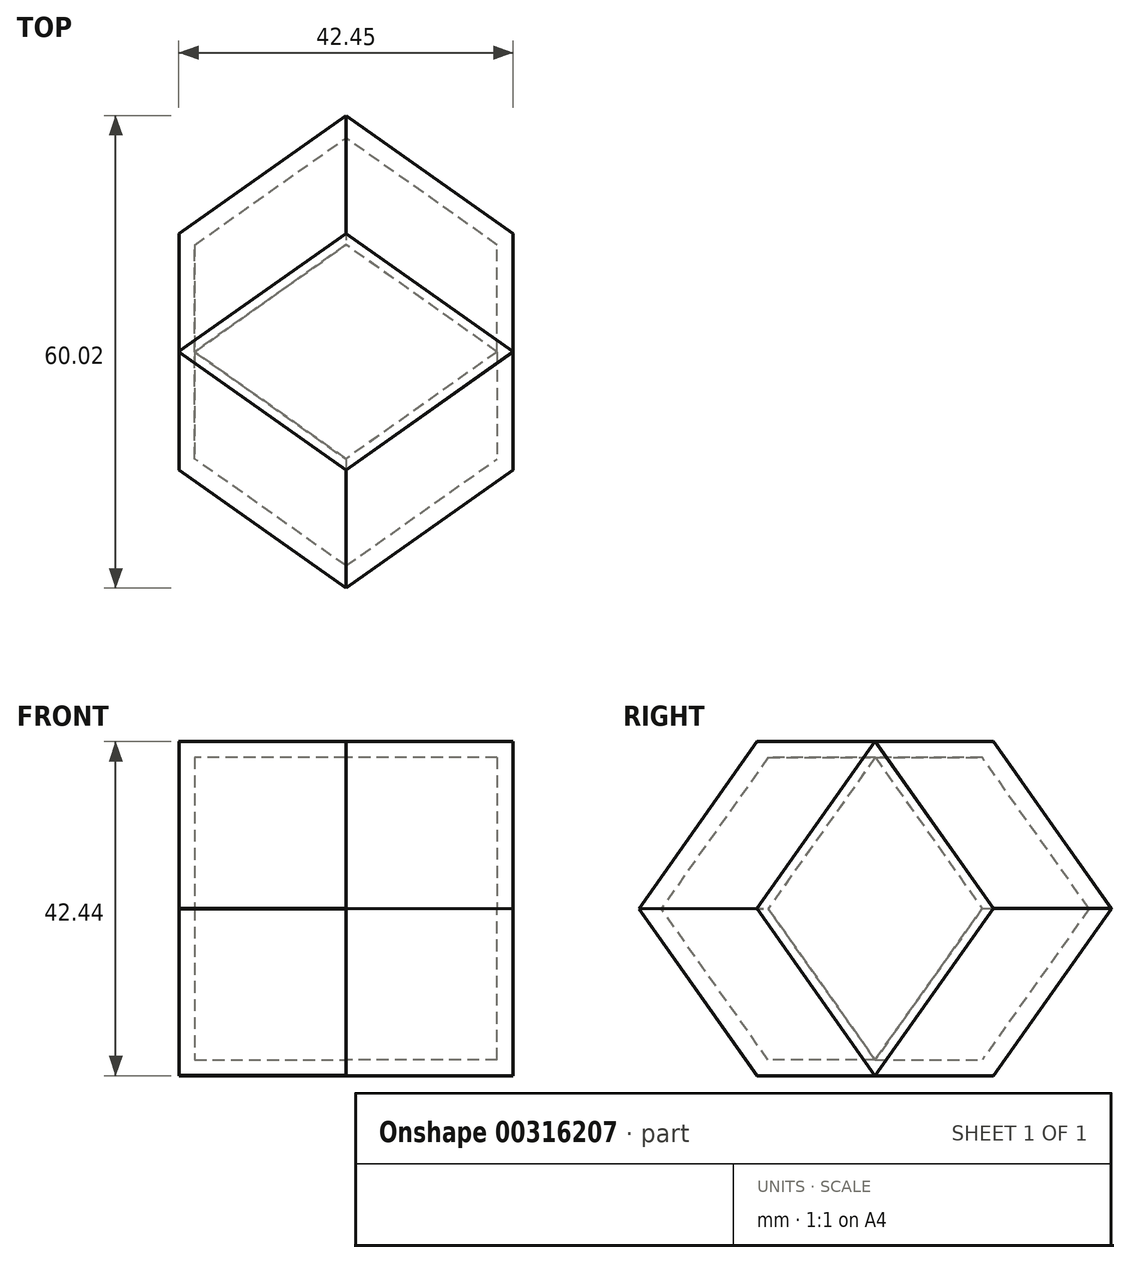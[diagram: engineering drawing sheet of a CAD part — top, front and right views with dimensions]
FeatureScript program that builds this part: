
annotation { "Feature Type Name" : "Feature", "Feature Type Description" : "" }
export const myFeature = defineFeature(function(context is Context, id is Id, definition is map)
    precondition{}
    {
        {
            var Q0;
            Q0=qCreatedBy(makeId("Top.planeOp"),FACE);
            var sketch = newSketch(context, id + "F0", { "sketchPlane" : qUnion([Q0])});
            skLineSegment(sketch, "E0", {"start": v(0, 15) * mm, "end": v(-21.22, 0) * mm});
            skLineSegment(sketch, "E1", {"start": v(-21.22, 0) * mm, "end": v(0, -15) * mm});
            skLineSegment(sketch, "E2", {"start": v(0, -15) * mm, "end": v(21.22, 0) * mm});
            skLineSegment(sketch, "E3", {"start": v(21.22, 0) * mm, "end": v(0, 15) * mm});
            skSolve(sketch);
        }
        {
            var Q0;
            Q0 = qSketchRegion(id + "F0", true);
            extrude(context, id + "F1", {"entities" : qUnion([Q0]), "depth" : 2 * mm, "hasDraft" : true, "draftAngle" : 15 * degree, "draftPullDirection" : true});
        }
        {
            var Q0;
            Q0=qCreatedBy(makeId("Right.planeOp"),FACE);
            var Q1;
            Q1=makeQuery(id+"F1.opExtrude","CAP_VERTEX",VERTEX,{"disambiguationData":[OSD([sQuery(id+"F0.wireOp",EDGE,"E2"),sQuery(id+"F0.wireOp",EDGE,"E3")])],"isStart":true});
            cPlane(context, id + "F2", {"entities" : qUnion([Q0, Q1]), "cplaneType" : CPlaneType.PLANE_POINT, "offset" : 25 * mm, "width" : 150 * mm, "height" : 150 * mm});
        }
        {
            var Q0;
            Q0=qCreatedBy(id+"F2.planeOp",FACE);
            var sketch = newSketch(context, id + "F3", { "sketchPlane" : qUnion([Q0])});
            skLineSegment(sketch, "E4.0", {"start": v(0, 0) * mm, "end": v(15, 0) * mm, "construction": true});
            skLineSegment(sketch, "E5", {"start": v(0, 0) * mm, "end": v(0, 42.44) * mm, "construction": true});
            skLineSegment(sketch, "E6", {"start": v(0, 0) * mm, "end": v(15, 21.22) * mm});
            skLineSegment(sketch, "E7", {"start": v(15, 21.22) * mm, "end": v(0, 42.44) * mm});
            skLineSegment(sketch, "E8", {"start": v(15, 21.22) * mm, "end": v(-15, 21.22) * mm, "construction": true});
            skLineSegment(sketch, "E9", {"start": v(0, 0) * mm, "end": v(-15, 21.22) * mm});
            skLineSegment(sketch, "E10", {"start": v(-15, 21.22) * mm, "end": v(0, 42.44) * mm});
            skSolve(sketch);
        }
        {
            var Q0;
            Q0 = qSketchRegion(id + "F3", true);
            extrude(context, id + "F4", {"entities" : qUnion([Q0]), "operationType" : NewBodyOperationType.ADD, "oppositeDirection" : true, "depth" : 2 * mm, "hasDraft" : true, "draftAngle" : 15 * degree, "draftPullDirection" : true});
        }
        {
            var Q0;
            Q0=makeQuery(id+"F1.opExtrude","CAP_VERTEX",VERTEX,{"disambiguationData":[OSD([sQuery(id+"F0.wireOp",EDGE,"E2"),sQuery(id+"F0.wireOp",EDGE,"E3")])],"isStart":true});
            var Q1;
            Q1=makeQuery(id+"F4.opExtrude","CAP_VERTEX",VERTEX,{"disambiguationData":[OSD([sQuery(id+"F3.wireOp",EDGE,"E9"),sQuery(id+"F3.wireOp",EDGE,"E10")])],"isStart":true});
            var Q2;
            Q2=makeQuery(id+"F1.opExtrude","CAP_VERTEX",VERTEX,{"disambiguationData":[OSD([sQuery(id+"F0.wireOp",EDGE,"E1"),sQuery(id+"F0.wireOp",EDGE,"E2")])],"isStart":true});
            cPlane(context, id + "F5", {"entities" : qUnion([Q0, Q1, Q2]), "cplaneType" : CPlaneType.THREE_POINT, "offset" : 25 * mm, "width" : 150 * mm, "height" : 150 * mm});
        }
        {
            var Q0;
            Q0=qCreatedBy(id+"F5.planeOp",FACE);
            var sketch = newSketch(context, id + "F6", { "sketchPlane" : qUnion([Q0])});
            skLineSegment(sketch, "E11.0", {"start": v(-18.38, 0) * mm, "end": v(-18.38, 25.99) * mm});
            skLineSegment(sketch, "E12.0", {"start": v(6.12, 8.66) * mm, "end": v(-18.38, 0) * mm});
            skLineSegment(sketch, "E13", {"start": v(-18.38, 25.99) * mm, "end": v(6.12, 8.66) * mm, "construction": true});
            skLineSegment(sketch, "E14", {"start": v(-18.38, 25.99) * mm, "end": v(6.12, 34.64) * mm});
            skLineSegment(sketch, "E15", {"start": v(6.12, 34.64) * mm, "end": v(6.12, 8.66) * mm});
            skSolve(sketch);
        }
        {
            var Q0;
            Q0 = qSketchRegion(id + "F6", true);
            extrude(context, id + "F7", {"entities" : qUnion([Q0]), "operationType" : NewBodyOperationType.ADD, "depth" : 2 * mm, "hasDraft" : true, "draftAngle" : 15 * degree, "draftPullDirection" : true});
        }
        {
            var Q0;
            Q0=makeQuery(id+"F7.boolean.opBoolean","MERGE",VERTEX,{"derivedFrom":[makeQuery(id+"F4.boolean.opBoolean","MERGE",VERTEX,{"derivedFrom":[makeQuery(id+"F1.opExtrude","CAP_VERTEX",VERTEX,{"disambiguationData":[OSD([sQuery(id+"F0.wireOp",EDGE,"E2"),sQuery(id+"F0.wireOp",EDGE,"E3")])],"isStart":true}),makeQuery(id+"F4.opExtrude","CAP_VERTEX",VERTEX,{"disambiguationData":[OSD([sQuery(id+"F3.wireOp",EDGE,"E6"),sQuery(id+"F3.wireOp",EDGE,"E9")])],"isStart":true})]}),makeQuery(id+"F7.opExtrude","CAP_VERTEX",VERTEX,{"disambiguationData":[OSD([sQuery(id+"F6.wireOp",EDGE,"E11.0"),sQuery(id+"F6.wireOp",EDGE,"E12.0")])],"isStart":true})]});
            var Q1;
            Q1=makeQuery(id+"F4.opExtrude","CAP_VERTEX",VERTEX,{"disambiguationData":[OSD([sQuery(id+"F3.wireOp",EDGE,"E6"),sQuery(id+"F3.wireOp",EDGE,"E7")])],"isStart":true});
            var Q2;
            Q2=makeQuery(id+"F1.opExtrude","CAP_VERTEX",VERTEX,{"disambiguationData":[OSD([sQuery(id+"F0.wireOp",EDGE,"E0"),sQuery(id+"F0.wireOp",EDGE,"E3")])],"isStart":true});
            cPlane(context, id + "F8", {"entities" : qUnion([Q0, Q1, Q2]), "cplaneType" : CPlaneType.THREE_POINT, "offset" : 25 * mm, "width" : 150 * mm, "height" : 150 * mm});
        }
        {
            var Q0;
            Q0=qCreatedBy(id+"F8.planeOp",FACE);
            var sketch = newSketch(context, id + "F9", { "sketchPlane" : qUnion([Q0])});
            skLineSegment(sketch, "E16.0", {"start": v(-18.38, 0) * mm, "end": v(6.12, 8.66) * mm});
            skLineSegment(sketch, "E17.0", {"start": v(-18.38, 0) * mm, "end": v(-18.38, 25.99) * mm});
            skLineSegment(sketch, "E18", {"start": v(6.12, 8.66) * mm, "end": v(6.12, 34.64) * mm});
            skLineSegment(sketch, "E19", {"start": v(6.12, 34.64) * mm, "end": v(-18.38, 25.99) * mm});
            skSolve(sketch);
        }
        {
            var Q0;
            Q0=makeQuery(id+"F9.imprint","IMPRINT",FACE,{"disambiguationData":[TD([[makeQuery(id+"F9.imprint","IMPRINT",EDGE,{"derivedFrom":sQuery(id+"F9.wireOp",EDGE,"E16.0")}),1.0]])]});
            extrude(context, id + "F10", {"entities" : qUnion([Q0]), "operationType" : NewBodyOperationType.ADD, "oppositeDirection" : true, "depth" : 2 * mm, "hasDraft" : true, "draftAngle" : 15 * degree, "draftPullDirection" : true});
        }
        {
            var Q0;
            Q0=makeQuery(id+"F10.opExtrude","CAP_VERTEX",VERTEX,{"disambiguationData":[OSD([sQuery(id+"F9.wireOp",EDGE,"E18"),sQuery(id+"F9.wireOp",EDGE,"E19")])],"isStart":true});
            var Q1;
            Q1=qCreatedBy(id+"F5.planeOp",FACE);
            cPlane(context, id + "F11", {"entities" : qUnion([Q0, Q1]), "cplaneType" : CPlaneType.PLANE_POINT, "offset" : 25 * mm, "width" : 150 * mm, "height" : 150 * mm});
        }
        {
            var Q0;
            Q0=qCreatedBy(id+"F11.planeOp",FACE);
            var sketch = newSketch(context, id + "F12", { "sketchPlane" : qUnion([Q0])});
            skLineSegment(sketch, "E20.0.0", {"start": v(6.12, 34.64) * mm, "end": v(6.12, 8.66) * mm});
            skLineSegment(sketch, "E20.0.1", {"start": v(6.12, 8.66) * mm, "end": v(-18.38, 0) * mm});
            skLineSegment(sketch, "E20.0.2", {"start": v(-18.38, 0) * mm, "end": v(-18.38, 25.99) * mm});
            skLineSegment(sketch, "E20.0.3", {"start": v(-18.38, 25.99) * mm, "end": v(6.12, 34.64) * mm});
            skSolve(sketch);
        }
        {
            var Q0;
            Q0 = qSketchRegion(id + "F12", true);
            extrude(context, id + "F13", {"entities" : qUnion([Q0]), "operationType" : NewBodyOperationType.ADD, "oppositeDirection" : true, "depth" : 2 * mm, "hasDraft" : true, "draftAngle" : 15 * degree, "draftPullDirection" : true});
        }
        {
            var Q0;
            Q0=qCreatedBy(id+"F8.planeOp",FACE);
            var Q1;
            Q1=makeQuery(id+"F7.opExtrude","CAP_VERTEX",VERTEX,{"disambiguationData":[OSD([sQuery(id+"F6.wireOp",EDGE,"E14"),sQuery(id+"F6.wireOp",EDGE,"E15")])],"isStart":true});
            cPlane(context, id + "F14", {"entities" : qUnion([Q0, Q1]), "cplaneType" : CPlaneType.PLANE_POINT, "offset" : 25 * mm, "width" : 150 * mm, "height" : 150 * mm});
        }
        {
            var Q0;
            Q0=qCreatedBy(id+"F14.planeOp",FACE);
            var sketch = newSketch(context, id + "F15", { "sketchPlane" : qUnion([Q0])});
            skLineSegment(sketch, "E21.0.0", {"start": v(6.12, 34.63) * mm, "end": v(6.1, 34.62) * mm});
            skLineSegment(sketch, "E21.0.1", {"start": v(6.1, 34.62) * mm, "end": v(6.11, 34.64) * mm});
            skLineSegment(sketch, "E21.0.2", {"start": v(6.11, 34.64) * mm, "end": v(-18.38, 25.99) * mm});
            skLineSegment(sketch, "E21.0.3", {"start": v(-18.38, 25.99) * mm, "end": v(-18.38, 0) * mm});
            skLineSegment(sketch, "E21.0.4", {"start": v(-18.38, 0) * mm, "end": v(6.12, 8.66) * mm});
            skLineSegment(sketch, "E21.0.5", {"start": v(6.12, 8.66) * mm, "end": v(6.12, 34.63) * mm});
            skSolve(sketch);
        }
        {
            var Q0;
            Q0 = qSketchRegion(id + "F15", true);
            extrude(context, id + "F16", {"entities" : qUnion([Q0]), "operationType" : NewBodyOperationType.ADD, "depth" : 2 * mm, "hasDraft" : true, "draftAngle" : 15 * degree, "draftPullDirection" : true});
        }
        {
            var Q0;
            Q0=makeQuery(id+"F13.opExtrude","CAP_VERTEX",VERTEX,{"disambiguationData":[OSD([sQuery(id+"F12.wireOp",EDGE,"E20.0.0"),sQuery(id+"F12.wireOp",EDGE,"E20.0.3")])],"isStart":true});
            var Q1;
            Q1=makeQuery(id+"F4.opExtrude","CAP_VERTEX",VERTEX,{"disambiguationData":[OSD([sQuery(id+"F3.wireOp",EDGE,"E7"),sQuery(id+"F3.wireOp",EDGE,"E10")])],"isStart":true});
            var Q2;
            Q2=makeQuery(id+"F13.opExtrude","CAP_VERTEX",VERTEX,{"disambiguationData":[OSD([sQuery(id+"F12.wireOp",EDGE,"E20.0.2"),sQuery(id+"F12.wireOp",EDGE,"E20.0.3")])],"isStart":true});
            cPlane(context, id + "F17", {"entities" : qUnion([Q0, Q1, Q2]), "cplaneType" : CPlaneType.THREE_POINT, "offset" : 25 * mm, "width" : 150 * mm, "height" : 150 * mm});
        }
        {
            var Q0;
            Q0=qCreatedBy(id+"F17.planeOp",FACE);
            var sketch = newSketch(context, id + "F18", { "sketchPlane" : qUnion([Q0])});
            skLineSegment(sketch, "E22.0.0", {"start": v(0, 15) * mm, "end": v(21.22, 0) * mm});
            skLineSegment(sketch, "E22.0.1", {"start": v(-21.22, 0) * mm, "end": v(0, 15) * mm});
            skLineSegment(sketch, "E22.0.2", {"start": v(0, -15) * mm, "end": v(-21.22, 0) * mm});
            skLineSegment(sketch, "E22.0.3", {"start": v(21.22, 0) * mm, "end": v(0, -15) * mm});
            skSolve(sketch);
        }
        {
            var Q0;
            Q0 = qSketchRegion(id + "F18", true);
            extrude(context, id + "F19", {"entities" : qUnion([Q0]), "operationType" : NewBodyOperationType.ADD, "depth" : 2 * mm, "hasDraft" : true, "draftAngle" : 15 * degree, "draftPullDirection" : true});
        }
        {
            var Q0;
            Q0=makeQuery(id+"F4.opExtrude","CAP_VERTEX",VERTEX,{"disambiguationData":[OSD([sQuery(id+"F3.wireOp",EDGE,"E7"),sQuery(id+"F3.wireOp",EDGE,"E10")])],"isStart":true});
            var Q1;
            Q1=makeQuery(id+"F7.boolean.opBoolean","MERGE",VERTEX,{"derivedFrom":[makeQuery(id+"F4.opExtrude","CAP_VERTEX",VERTEX,{"disambiguationData":[OSD([sQuery(id+"F3.wireOp",EDGE,"E9"),sQuery(id+"F3.wireOp",EDGE,"E10")])],"isStart":true}),makeQuery(id+"F7.opExtrude","CAP_VERTEX",VERTEX,{"disambiguationData":[OSD([sQuery(id+"F6.wireOp",EDGE,"E11.0"),sQuery(id+"F6.wireOp",EDGE,"E14")])],"isStart":true})]});
            var Q2;
            Q2=makeQuery(id+"F16.opExtrude","CAP_VERTEX",VERTEX,{"disambiguationData":[OSD([sQuery(id+"F15.wireOp",EDGE,"E21.0.3"),sQuery(id+"F15.wireOp",EDGE,"E21.0.4")])],"isStart":true});
            cPlane(context, id + "F20", {"entities" : qUnion([Q0, Q1, Q2]), "cplaneType" : CPlaneType.THREE_POINT, "offset" : 25 * mm, "width" : 150 * mm, "height" : 150 * mm});
        }
        {
            var Q0;
            Q0=qCreatedBy(id+"F20.planeOp",FACE);
            var sketch = newSketch(context, id + "F21", { "sketchPlane" : qUnion([Q0])});
            skLineSegment(sketch, "E23.0", {"start": v(6.12, 8.67) * mm, "end": v(6.12, 34.66) * mm});
            skLineSegment(sketch, "E24.0", {"start": v(-18.37, 25.99) * mm, "end": v(-18.37, 0) * mm});
            skLineSegment(sketch, "E25", {"start": v(-18.37, 25.99) * mm, "end": v(6.12, 34.66) * mm});
            skLineSegment(sketch, "E26", {"start": v(-18.37, 0) * mm, "end": v(6.12, 8.67) * mm});
            skSolve(sketch);
        }
        {
            var Q0;
            Q0 = qSketchRegion(id + "F21", true);
            extrude(context, id + "F22", {"entities" : qUnion([Q0]), "operationType" : NewBodyOperationType.ADD, "oppositeDirection" : true, "depth" : 2 * mm, "hasDraft" : true, "draftAngle" : 15 * degree, "draftPullDirection" : true});
        }
        {
            var Q0;
            Q0=makeQuery(id+"F1.opExtrude","CAP_VERTEX",VERTEX,{"disambiguationData":[OSD([sQuery(id+"F0.wireOp",EDGE,"E0"),sQuery(id+"F0.wireOp",EDGE,"E1")])],"isStart":true});
            var Q1;
            Q1=makeQuery(id+"F4.opExtrude","CAP_FACE",FACE,{"disambiguationData":[OSD([sQuery(id+"F3.wireOp",EDGE,"E6"),sQuery(id+"F3.wireOp",EDGE,"E7"),sQuery(id+"F3.wireOp",EDGE,"E9"),sQuery(id+"F3.wireOp",EDGE,"E10")])],"isStart":true});
            cPlane(context, id + "F23", {"entities" : qUnion([Q0, Q1]), "cplaneType" : CPlaneType.PLANE_POINT, "offset" : 25 * mm, "width" : 150 * mm, "height" : 150 * mm});
        }
        {
            var Q0;
            Q0=qCreatedBy(id+"F23.planeOp",FACE);
            var sketch = newSketch(context, id + "F24", { "sketchPlane" : qUnion([Q0])});
            skLineSegment(sketch, "E27.0.0", {"start": v(-15, 21.22) * mm, "end": v(0, 42.44) * mm});
            skLineSegment(sketch, "E27.0.1", {"start": v(0, 0) * mm, "end": v(-15, 21.22) * mm});
            skLineSegment(sketch, "E27.0.2", {"start": v(0, 0) * mm, "end": v(15, 21.22) * mm});
            skLineSegment(sketch, "E27.0.3", {"start": v(15, 21.22) * mm, "end": v(0, 42.44) * mm});
            skSolve(sketch);
        }
        {
            var Q0;
            Q0 = qSketchRegion(id + "F24", true);
            extrude(context, id + "F25", {"entities" : qUnion([Q0]), "operationType" : NewBodyOperationType.ADD, "depth" : 2 * mm, "hasDraft" : true, "draftAngle" : 15 * degree, "draftPullDirection" : true});
        }
        {
            var Q0;
            Q0=makeQuery(id+"F22.opExtrude","CAP_FACE",FACE,{"disambiguationData":[OSD([sQuery(id+"F21.wireOp",EDGE,"E23.0"),sQuery(id+"F21.wireOp",EDGE,"E24.0"),sQuery(id+"F21.wireOp",EDGE,"E25"),sQuery(id+"F21.wireOp",EDGE,"E26")])],"isStart":true});
            var Q1;
            Q1=makeQuery(id+"F25.boolean.opBoolean","MERGE",VERTEX,{"derivedFrom":[makeQuery(id+"F1.opExtrude","CAP_VERTEX",VERTEX,{"disambiguationData":[OSD([sQuery(id+"F0.wireOp",EDGE,"E0"),sQuery(id+"F0.wireOp",EDGE,"E1")])],"isStart":true}),makeQuery(id+"F25.opExtrude","CAP_VERTEX",VERTEX,{"disambiguationData":[OSD([sQuery(id+"F24.wireOp",EDGE,"E27.0.1"),sQuery(id+"F24.wireOp",EDGE,"E27.0.2")])],"isStart":true})]});
            cPlane(context, id + "F26", {"entities" : qUnion([Q0, Q1]), "cplaneType" : CPlaneType.PLANE_POINT, "offset" : 25 * mm, "width" : 150 * mm, "height" : 150 * mm});
        }
        {
            var Q0;
            Q0=qCreatedBy(id+"F26.planeOp",FACE);
            var sketch = newSketch(context, id + "F27", { "sketchPlane" : qUnion([Q0])});
            skLineSegment(sketch, "E28.0", {"start": v(-18.37, 0) * mm, "end": v(-18.37, 25.99) * mm});
            skLineSegment(sketch, "E29.0", {"start": v(6.13, 8.66) * mm, "end": v(6.13, 34.63) * mm});
            skLineSegment(sketch, "E30", {"start": v(6.13, 34.63) * mm, "end": v(-18.37, 25.99) * mm});
            skLineSegment(sketch, "E31", {"start": v(6.13, 8.66) * mm, "end": v(-18.37, 0) * mm});
            skSolve(sketch);
        }
        {
            var Q0;
            Q0 = qSketchRegion(id + "F27", true);
            extrude(context, id + "F28", {"entities" : qUnion([Q0]), "operationType" : NewBodyOperationType.ADD, "depth" : 2 * mm, "hasDraft" : true, "draftAngle" : 15 * degree, "draftPullDirection" : true});
        }
        {
            var Q0;
            Q0=makeQuery(id+"F13.opExtrude","CAP_VERTEX",VERTEX,{"disambiguationData":[OSD([sQuery(id+"F12.wireOp",EDGE,"E20.0.2"),sQuery(id+"F12.wireOp",EDGE,"E20.0.3")])],"isStart":true});
            var Q1;
            Q1=makeQuery(id+"F19.opExtrude","CAP_VERTEX",VERTEX,{"disambiguationData":[OSD([sQuery(id+"F18.wireOp",EDGE,"E22.0.0"),sQuery(id+"F18.wireOp",EDGE,"E22.0.3")])],"isStart":true});
            var Q2;
            Q2=makeQuery(id+"F10.boolean.opBoolean","MERGE",VERTEX,{"derivedFrom":[makeQuery(id+"F4.opExtrude","CAP_VERTEX",VERTEX,{"disambiguationData":[OSD([sQuery(id+"F3.wireOp",EDGE,"E6"),sQuery(id+"F3.wireOp",EDGE,"E7")])],"isStart":true}),makeQuery(id+"F10.opExtrude","CAP_VERTEX",VERTEX,{"disambiguationData":[OSD([sQuery(id+"F9.wireOp",EDGE,"E17.0"),sQuery(id+"F9.wireOp",EDGE,"E19")])],"isStart":true})]});
            cPlane(context, id + "F29", {"entities" : qUnion([Q0, Q1, Q2]), "cplaneType" : CPlaneType.THREE_POINT, "offset" : 25 * mm, "width" : 150 * mm, "height" : 150 * mm});
        }
        {
            var Q0;
            Q0=qCreatedBy(id+"F29.planeOp",FACE);
            var sketch = newSketch(context, id + "F30", { "sketchPlane" : qUnion([Q0])});
            skLineSegment(sketch, "E32.0", {"start": v(6.12, 34.65) * mm, "end": v(-18.37, 26) * mm});
            skLineSegment(sketch, "E33.0", {"start": v(-18.37, 0.02) * mm, "end": v(6.13, 8.67) * mm});
            skLineSegment(sketch, "E34", {"start": v(6.12, 34.65) * mm, "end": v(6.13, 8.67) * mm});
            skLineSegment(sketch, "E35", {"start": v(-18.37, 26) * mm, "end": v(-18.37, 0.02) * mm});
            skSolve(sketch);
        }
        {
            var Q0;
            Q0 = qSketchRegion(id + "F30", true);
            extrude(context, id + "F31", {"entities" : qUnion([Q0]), "operationType" : NewBodyOperationType.ADD, "depth" : 2 * mm, "hasDraft" : true, "draftAngle" : 15 * degree, "draftPullDirection" : true});
        }
        {
            var Q0;
            Q0=qCreatedBy(id+"F29.planeOp",FACE);
            var Q1;
            Q1=makeQuery(id+"F22.boolean.opBoolean","MERGE",VERTEX,{"derivedFrom":[makeQuery(id+"F16.opExtrude","CAP_VERTEX",VERTEX,{"disambiguationData":[OSD([sQuery(id+"F15.wireOp",EDGE,"E21.0.3"),sQuery(id+"F15.wireOp",EDGE,"E21.0.4")])],"isStart":true}),makeQuery(id+"F22.opExtrude","CAP_VERTEX",VERTEX,{"disambiguationData":[OSD([sQuery(id+"F21.wireOp",EDGE,"E24.0"),sQuery(id+"F21.wireOp",EDGE,"E26")])],"isStart":true})]});
            cPlane(context, id + "F32", {"entities" : qUnion([Q0, Q1]), "cplaneType" : CPlaneType.PLANE_POINT, "offset" : 25 * mm, "width" : 150 * mm, "height" : 150 * mm});
        }
        {
            var Q0;
            Q0=qCreatedBy(id+"F32.planeOp",FACE);
            var sketch = newSketch(context, id + "F33", { "sketchPlane" : qUnion([Q0])});
            skLineSegment(sketch, "E36.0.4", {"start": v(6.12, 34.65) * mm, "end": v(-18.37, 26) * mm});
            skLineSegment(sketch, "E36.0.5", {"start": v(6.12, 34.65) * mm, "end": v(6.13, 8.67) * mm});
            skLineSegment(sketch, "E36.0.6", {"start": v(-18.37, 0.02) * mm, "end": v(6.13, 8.67) * mm});
            skLineSegment(sketch, "E37", {"start": v(-18.37, 0.02) * mm, "end": v(-18.37, 26) * mm});
            skSolve(sketch);
        }
        {
            var Q0;
            Q0 = qSketchRegion(id + "F33", true);
            extrude(context, id + "F34", {"entities" : qUnion([Q0]), "operationType" : NewBodyOperationType.ADD, "oppositeDirection" : true, "depth" : 2 * mm, "hasDraft" : true, "draftAngle" : 15 * degree, "draftPullDirection" : true});
        }
    });
